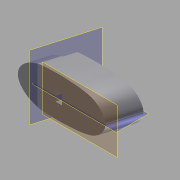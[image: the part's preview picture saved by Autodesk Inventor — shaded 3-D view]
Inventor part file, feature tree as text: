
AUTODESK INVENTOR PART (.ipt)
format: ipt  version: 2012 SP2 (Build 160219200, 219)  size: 425,472 bytes
history: native  units: in
note: dims shown in document units (in); Inventor stores cm internally (conversion verified against a paired STEP export)
features: sketch x14, sweep x5, plane x4, extrude x2, other x2, mirror x1, projected_geometry x1, surface_op x1
ambient origin geometry x8: Origin, YZ Plane, XZ Plane, XY Plane, X Axis, Y Axis, Z Axis, Center Point
bodies: Solid1 (feature_tree)
feature tree (30):
  sketch  "Sketch1"  dims[d6=0.9405in d9=0.688in]
  plane  "Work Plane1"
  plane  "Work Plane2"
  sketch  "Sketch3"  dims[d12=0.2381in d13=0.5734in]
  plane  "Work Plane3"
  sweep  "Sweep1"
  sweep  "Sweep2"
  extrude  "Extrusion1"  Depth=0.5734in
  plane  "Work Plane4"
  mirror  "Mirror1"
  sweep  "Sweep3"
  sweep  "Sweep5"
  sweep  "Sweep7"
  extrude  "Extrusion3"  Depth=0.7769in
  other  "Image1"
  sketch  "Sketch2"  dims[d10=0.069in d11=0.12in]
  other  "Srf1"
  sketch  "Sketch4"  dims[d14=0.4256in d15=1.588in]
  sketch  "Sketch5"  dims[d16=0.3503in d17=0.5806in]
  sketch  "Sketch6"  dims[d18=0.3426in d19=0.2058in]
  sketch  "Sketch7"  dims[d20=0.3395in d21=0.7769in]
  sketch  "Sketch8"  dims[d22=0.3374in]
  sketch  "Sketch9"  dims[d23=0.1206in]
  sketch  "Sketch10"  dims[d24=0.3329in]
  sketch  "Sketch14"  dims[d25=0.8673in]
  sketch  "Sketch18"  dims[d26=0.3313in]
  sketch  "3D Sketch1"
  sketch  "Sketch19"  dims[d27=0.0621in d28=0.323in d29=0.9887in d30=0.2944in d31=1.1563in d32=0.2583in d33=1.2792in d34=0.1988in d35=1.391in d36=0.1269in d37=1.4752in d38=0.0171in d39=1.5524in d40=0.0519in d41=1.5805in d42=0.1042in d43=1.7561in d44=0.2965in d47=0.5902in d48=0.2in d49=0.0in d50=0.6495in d51=1.035in d52=0.5105in d53=0.306in d54=0.5955in d55=0.0in d56=0.6605in d57=0.053in d58=0.1095in d59=0.2in d60=0.055in d61=0.0in d62=0.7687in d64=0.3167in d65=0.4475in d66=0.0in d67=0.0285in d68=0.0285in d69=0.0285in d70=0.0285in d71=0.0285in d72=0.0285in d76=0.0in d84=0.0in d85=0.3in d86=0.0in]
  projected_geometry  "Projected Loop2"
  surface_op  "Boundary Patch1"
